# Revit family: Faucet-Manual-American_Standard-Monterrey-55001X5_Series.rfaxx
name_source: partatom
category: Plumbing Fixtures
units: mm (PartAtom-declared; Revit-internal decimal feet)

## family parameters
Always vertical = No
Cut with Voids When Loaded = No
OmniClass Number = 23.45.55.17
OmniClass Title = Mixing Faucets
Part Type = Normal
Room Calculation Point = No
Round Connector Dimension = Use Diameter
Shared = Yes
Work Plane-Based = Yes

## types (3) — shared parameters
ADA Compliant = Yes
Assembly Code = D2020300
CEC Compliant = Yes
CW Connection = Yes
CWFU = 1.5
CalGreen Compliant = Yes
Cold Water Connection Diameter = 1/2"
Compliance Certifications = Water Efficient, ANSI A117.1, ASME A112.18.1, CSA B 125, NSF 372
Default Elevation = 0"
Finish = Brass-American Standard-002-Polished Chrome
Flow Rate = 0.5 gpm/1.9 Lpm
HW Connection = Yes
HWFU = 1.5
Height = 2 3/4"
Hot Water Connection Diameter = 1"
Installation Type = Deck Mounted
Length = 3 3/4"
Manufacturer = American Standard
Material = Brass-American Standard-002-Polished Chrome
Price = Prices may vary. Please consult Manufacturer Representative for most up-to-date price list.
Product Documentation Link = https://americanstandard.box.com
Revised Date = 02/02/2023
Vent Connection = No
WFU = 2
Warranty Information = 5  Year Limited Warranty
Waste Connection = No

## per-type parameters (varying)
| type | Description | Grid Drain Included | Lever Handles | Overall Width | Product Page URL | URL | Wrist Blade Handles |
| 5502.175.002 | Monterrey® 4-Inch Centerset Cast Faucet With Wrist Blade Handles 0.5 gpm/1.9 Lpm With Grid Drain | Yes | No | 11 3/4" | https://www.americanstandard.ca | https://www.americanstandard.ca | Yes |
| 5500.175.002 | Monterrey® 4-Inch Centerset Cast Faucet With Wrist Blade Handles 0.5 gpm/1.9 Lpm | No | No | 11 3/4" | https://www.americanstandard-us.com | https://www.americanstandard-us.com | Yes |
| 5500.145.002 | Monterrey® 4-Inch Centerset Cast Faucet With Lever Handles 0.5 gpm/1.9 Lpm | No | Yes | 8 1/2" | https://www.americanstandard-us.com | https://www.americanstandard.ca | No |

note: column(s) folded — value = type name in every type: Model

## geometry (parser evidence)
native form markers: Sweep x2
no freeform markers — native parametric forms only
